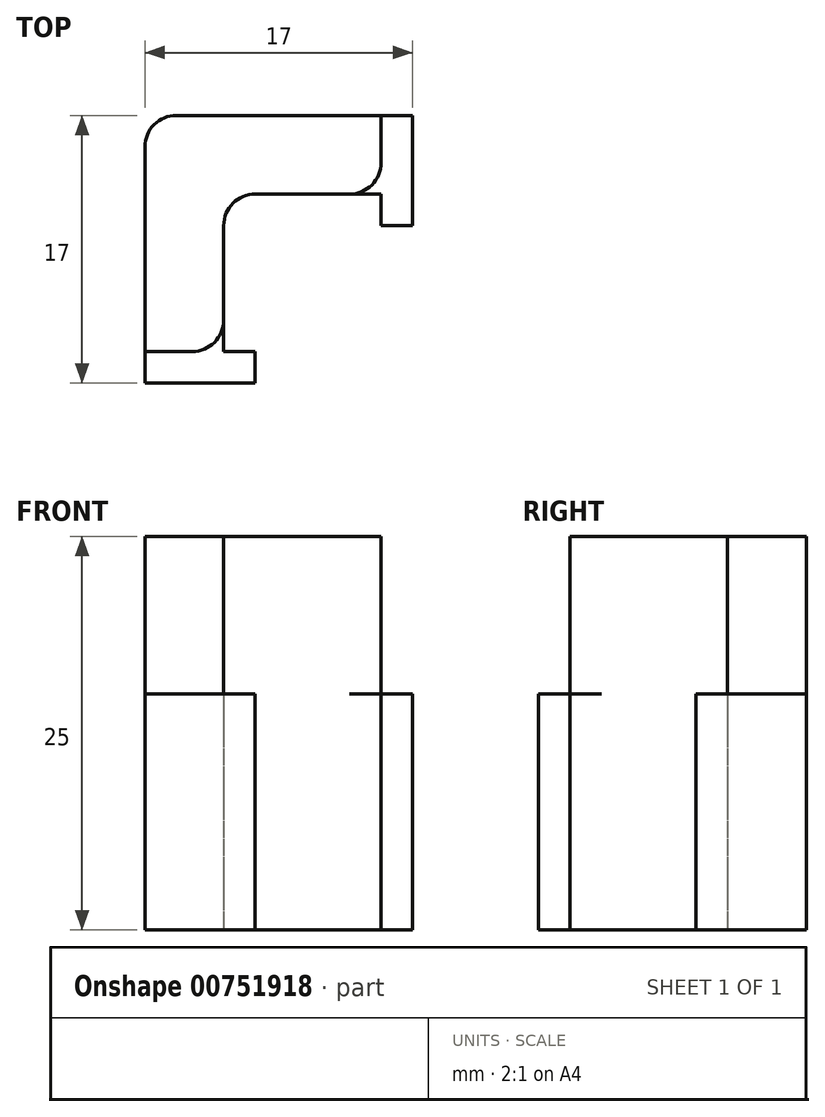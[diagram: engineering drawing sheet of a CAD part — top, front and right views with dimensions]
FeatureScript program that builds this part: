
annotation { "Feature Type Name" : "Feature", "Feature Type Description" : "" }
export const myFeature = defineFeature(function(context is Context, id is Id, definition is map)
    precondition{}
    {
        {
            var Q0;
            Q0=qCreatedBy(makeId("Top.planeOp"),FACE);
            var sketch = newSketch(context, id + "F0", { "sketchPlane" : qUnion([Q0])});
            skLineSegment(sketch, "E0.bottom", {"start": v(0, 0) * mm, "end": v(15, 0) * mm});
            skLineSegment(sketch, "E0.top", {"start": v(0, -15) * mm, "end": v(5, -15) * mm});
            skLineSegment(sketch, "E0.left", {"start": v(0, 0) * mm, "end": v(0, -15) * mm});
            skLineSegment(sketch, "E0.right", {"start": v(15, 0) * mm, "end": v(15, -5) * mm});
            skLineSegment(sketch, "E1.0", {"start": v(5, -5) * mm, "end": v(15, -5) * mm});
            skLineSegment(sketch, "E2.0", {"start": v(5, -5) * mm, "end": v(5, -15) * mm});
            skLineSegment(sketch, "E3.bottom", {"start": v(15, 0) * mm, "end": v(17, 0) * mm});
            skLineSegment(sketch, "E3.top", {"start": v(15, -7) * mm, "end": v(17, -7) * mm});
            skLineSegment(sketch, "E3.left", {"start": v(15, 0) * mm, "end": v(15, -7) * mm});
            skLineSegment(sketch, "E3.right", {"start": v(17, 0) * mm, "end": v(17, -7) * mm});
            skLineSegment(sketch, "E4.bottom", {"start": v(0, -15) * mm, "end": v(7, -15) * mm});
            skLineSegment(sketch, "E4.top", {"start": v(0, -17) * mm, "end": v(7, -17) * mm});
            skLineSegment(sketch, "E4.left", {"start": v(0, -15) * mm, "end": v(0, -17) * mm});
            skLineSegment(sketch, "E4.right", {"start": v(7, -15) * mm, "end": v(7, -17) * mm});
            skSolve(sketch);
        }
        {
            var Q0;
            Q0=makeQuery(id+"F0.imprint","IMPRINT",FACE,{"disambiguationData":[TD([[makeQuery(id+"F0.imprint","IMPRINT",EDGE,{"derivedFrom":sQuery(id+"F0.wireOp",EDGE,"E0.bottom")}),-1.0]])]});
            extrude(context, id + "F1", {"entities" : qUnion([Q0]), "depth" : 25 * mm, "offsetDistance" : 25 * mm});
        }
        {
            var Q0;
            Q0=makeQuery(id+"F1.opExtrude","SWEPT_EDGE",EDGE,{"disambiguationData":[OSD([sQuery(id+"F0.wireOp",EDGE,"E1.0"),sQuery(id+"F0.wireOp",EDGE,"E2.0")])]});
            var Q1;
            Q1=makeQuery(id+"F1.opExtrude","SWEPT_EDGE",EDGE,{"disambiguationData":[OSD([sQuery(id+"F0.wireOp",EDGE,"E0.bottom"),sQuery(id+"F0.wireOp",EDGE,"E0.left")])]});
            var Q2;
            Q2=makeQuery(id+"F1.opExtrude","SWEPT_EDGE",EDGE,{"disambiguationData":[OSD([sQuery(id+"F0.wireOp",EDGE,"E0.bottom"),sQuery(id+"F0.wireOp",EDGE,"E0.left")])]});
            var Q3;
            Q3=makeQuery(id+"F1.opExtrude","SWEPT_EDGE",EDGE,{"disambiguationData":[OSD([sQuery(id+"F0.wireOp",EDGE,"E0.bottom"),sQuery(id+"F0.wireOp",EDGE,"E0.left")])]});
            fillet(context, id + "F2", {"entities" : qUnion([Q0, Q1, Q2, Q3]), "radius" : 2 * mm, "tangentPropagation" : true, "allowEdgeOverflow" : false});
        }
        {
            var Q0;
            Q0=makeQuery(id+"F0.imprint","IMPRINT",FACE,{"disambiguationData":[TD([[makeQuery(id+"F0.imprint","IMPRINT",EDGE,{"derivedFrom":sQuery(id+"F0.wireOp",EDGE,"E0.top")}),-1.0]])]});
            var Q1;
            Q1=makeQuery(id+"F0.imprint","IMPRINT",FACE,{"disambiguationData":[TD([[makeQuery(id+"F0.imprint","IMPRINT",EDGE,{"derivedFrom":sQuery(id+"F0.wireOp",EDGE,"E0.right")}),1.0]])]});
            extrude(context, id + "F3", {"entities" : qUnion([Q0, Q1]), "operationType" : NewBodyOperationType.ADD, "depth" : 15 * mm, "offsetDistance" : 25 * mm});
        }
        {
            var Q0;
            {var subQ0=sQuery(id+"F0.wireOp",EDGE,"E2.0");var subQ1=sQuery(id+"F0.wireOp",EDGE,"E4.bottom");var subQ2=sQuery(id+"F0.wireOp",EDGE,"E0.top");Q0=makeQuery(id+"F3.boolean.opBoolean","SPLIT",EDGE,{"disambiguationData":[topologyDisambiguationEdgeConnected([makeQuery(id+"F3.opExtrude","SWEPT_FACE",FACE,{"disambiguationData":[OSD([subQ2,subQ1])]})])],"derivedFrom":makeQuery(id+"F1.opExtrude","SWEPT_EDGE",EDGE,{"disambiguationData":[OSD([subQ2,subQ0,subQ1])]})});}
            var Q1;
            {var subQ0=sQuery(id+"F0.wireOp",EDGE,"E1.0");var subQ1=sQuery(id+"F0.wireOp",EDGE,"E3.left");var subQ2=sQuery(id+"F0.wireOp",EDGE,"E0.right");Q1=makeQuery(id+"F3.boolean.opBoolean","SPLIT",EDGE,{"disambiguationData":[topologyDisambiguationEdgeConnected([makeQuery(id+"F3.opExtrude","SWEPT_FACE",FACE,{"disambiguationData":[OSD([subQ2,subQ1])]})])],"derivedFrom":makeQuery(id+"F1.opExtrude","SWEPT_EDGE",EDGE,{"disambiguationData":[OSD([subQ2,subQ0,subQ1])]})});}
            fillet(context, id + "F4", {"entities" : qUnion([Q0, Q1]), "radius" : 2 * mm, "tangentPropagation" : true, "allowEdgeOverflow" : false});
        }
    });
